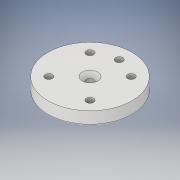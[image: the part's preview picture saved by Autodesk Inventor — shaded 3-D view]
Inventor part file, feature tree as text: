
AUTODESK INVENTOR PART (.ipt)
format: ipt  version: 2019 (Build 230136000, 136)  size: 167,936 bytes
history: native  units: in
note: dims shown in document units (in); Inventor stores cm internally (conversion verified against a paired STEP export)
features: sketch x4, extrude x3, fillet x2, hole x2
ambient origin geometry x8: Origin, YZ Plane, XZ Plane, XY Plane, X Axis, Y Axis, Z Axis, Center Point
bodies: Solid1 (feature_tree)
feature tree (11):
  extrude  "Extrusion1"  Depth=0.4331in TaperAngle=0.0deg
  fillet  "Fillet2"  Radius=0.0394in
  extrude  "Extrusion6"  Depth=0.3543in TaperAngle=0.0deg
  fillet  "Fillet4"  Radius=0.125in
  extrude  "Extrusion7"  Depth=0.6693in
  hole  "Hole5"  [1 undecoded]
  hole  "Hole6"  [1 undecoded]
  sketch  "Sketch1"  dims[d0=2.8346in d1=0.4331in d2=0.0in d36=0.0394in]
  sketch  "Sketch10"  dims[d66=1.1811in d67=0.3543in d68=0.0in d69=0.125in]
  sketch  "Sketch11"  dims[d70=0.748in d71=0.6693in]
  sketch  "Sketch12"  dims[d72=0.3346in d73=0.374in d74=0.374in d75=0.3543in d76=0.0in d77=0.2441in d78=0.146in d79=0.5291in d80=0.25in d81=90.0deg d82=1.0in d83=0.8108in d84=45.0deg d85=0.9843in d86=0.9843in d87=1.5748in d89=360.0deg d91=0.2441in d92=0.146in d93=0.5291in d94=0.25in d95=90.0deg d96=1.0in d97=0.8108in d20=1.0in d21=1.0in d22=1.0in d23=0.15in d24=0.25in d25=0.375in d26=0.5635in d27=0.75in d28=0.8108in d29=0.0625in d30=0.75in d31=0.375in]
note: 2 required parameter values undecoded (feature->parameter linkage not recoverable at this tier; creation-order binding heuristic only, values carry confidence <= 0.55)
